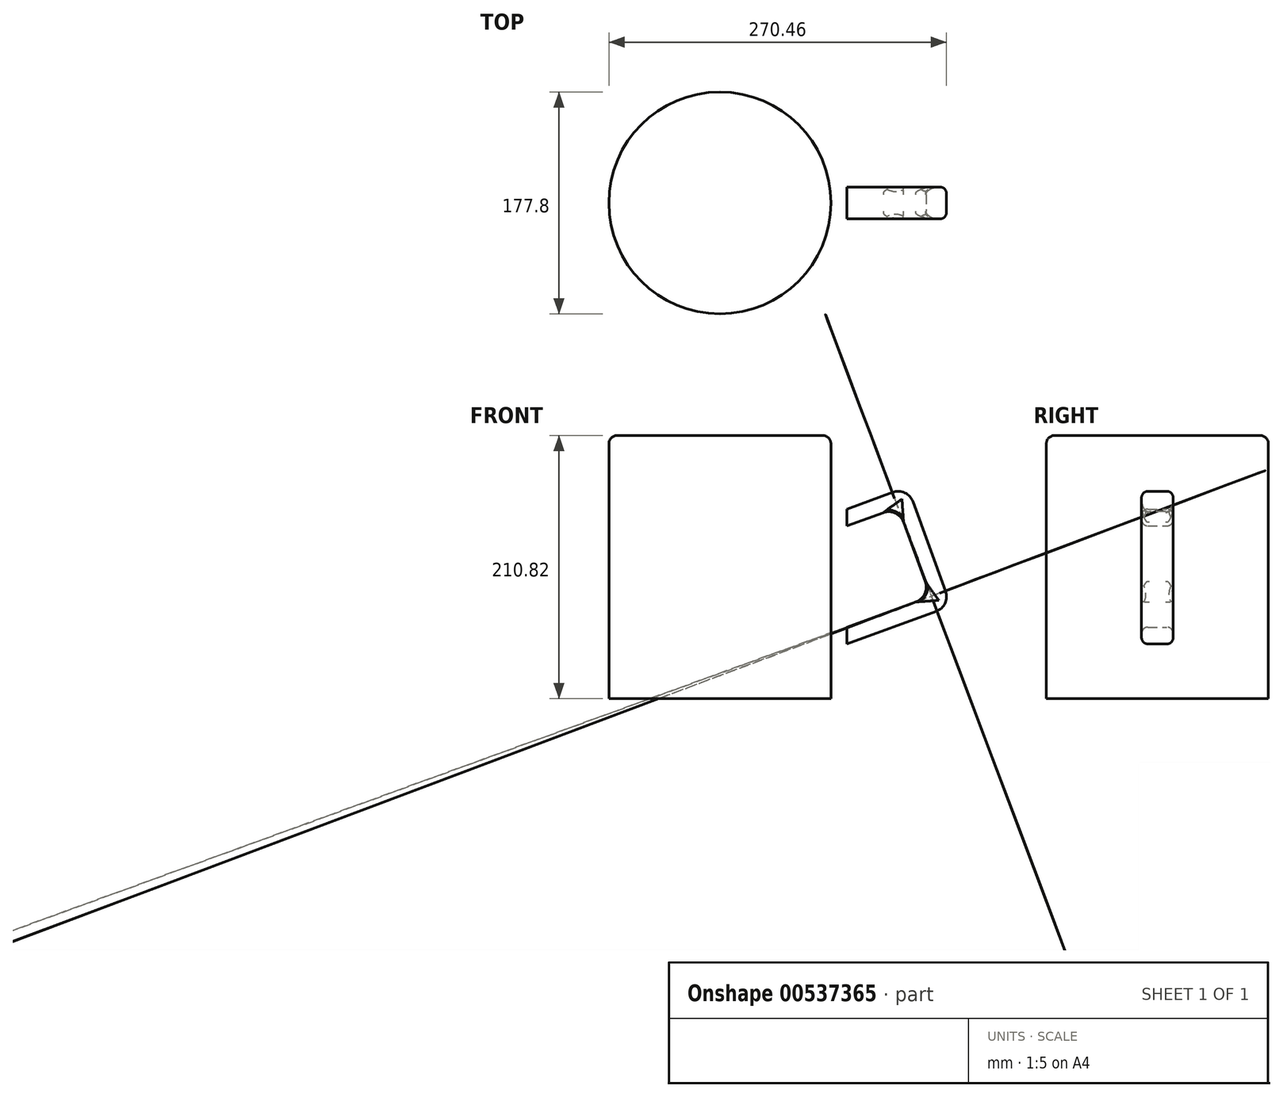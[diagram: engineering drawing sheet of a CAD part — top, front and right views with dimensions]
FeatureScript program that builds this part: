
annotation { "Feature Type Name" : "Feature", "Feature Type Description" : "" }
export const myFeature = defineFeature(function(context is Context, id is Id, definition is map)
    precondition{}
    {
        {
            var Q0;
            Q0=qCreatedBy(makeId("Front.planeOp"),FACE);
            var sketch = newSketch(context, id + "F0", { "sketchPlane" : qUnion([Q0])});
            skLineSegment(sketch, "E0.bottom", {"start": v(0, 114.3) * mm, "end": v(-101.6, 114.3) * mm});
            skLineSegment(sketch, "E0.top", {"start": v(0, -114.3) * mm, "end": v(-101.6, -114.3) * mm});
            skLineSegment(sketch, "E0.right", {"start": v(-101.6, 114.3) * mm, "end": v(-101.6, -114.3) * mm});
            skPoint(sketch, "E0.middle", {"position": v(0, 0) * mm});
            skLineSegment(sketch, "E1.bottom", {"start": v(-88.9, 114.3) * mm, "end": v(0, 114.3) * mm});
            skLineSegment(sketch, "E1.top", {"start": v(-88.9, -96.52) * mm, "end": v(0, -96.52) * mm});
            skLineSegment(sketch, "E1.left", {"start": v(-88.9, 114.3) * mm, "end": v(-88.9, -96.52) * mm});
            skLineSegment(sketch, "E2", {"start": v(0, 114.3) * mm, "end": v(0, -114.3) * mm});
            skPoint(sketch, "E0.left.end.orphan", {"position": v(101.6, -114.3) * mm});
            skPoint(sketch, "E3.orphan", {"position": v(101.6, 114.3) * mm});
            skSolve(sketch);
        }
        {
            var Q0;
            Q0=makeQuery(id+"F0.imprint","IMPRINT",FACE,{"disambiguationData":[TD([[makeQuery(id+"F0.imprint","IMPRINT",EDGE,{"derivedFrom":sQuery(id+"F0.wireOp",EDGE,"E0.bottom")}),1.0]])]});
            var Q1;
            Q1=sQuery(id+"F0.wireOp",EDGE,"E2");
            revolve(context, id + "F1", {"entities" : qUnion([Q0]), "axis" : qUnion([Q1]), "revolveType" : RevolveType.FULL});
        }
        {
            var Q0;
            Q0=makeQuery(id+"F1.opRevolve","SWEPT_EDGE",EDGE,{"disambiguationData":[OSD([sQuery(id+"F0.wireOp",EDGE,"E0.bottom"),sQuery(id+"F0.wireOp",EDGE,"E1.bottom"),sQuery(id+"F0.wireOp",EDGE,"E1.left")])]});
            var Q1;
            Q1=makeQuery(id+"F1.opRevolve","SWEPT_EDGE",EDGE,{"disambiguationData":[OSD([sQuery(id+"F0.wireOp",EDGE,"E0.bottom"),sQuery(id+"F0.wireOp",EDGE,"E0.right")])]});
            var Q2;
            Q2=makeQuery(id+"F1.opRevolve","SWEPT_EDGE",EDGE,{"disambiguationData":[OSD([sQuery(id+"F0.wireOp",EDGE,"E0.top"),sQuery(id+"F0.wireOp",EDGE,"E0.right")])]});
            fillet(context, id + "F2", {"entities" : qUnion([Q0, Q1, Q2]), "radius" : 6.35 * mm, "tangentPropagation" : true, "allowEdgeOverflow" : false});
        }
        {
            var Q0;
            Q0=qCreatedBy(makeId("Front.planeOp"),FACE);
            var sketch = newSketch(context, id + "F3", { "sketchPlane" : qUnion([Q0])});
            skLineSegment(sketch, "E4", {"start": v(101.6, 101.6) * mm, "end": v(101.6, -103.5) * mm});
            skLineSegment(sketch, "E5", {"start": v(-101.6, -101.6) * mm, "end": v(-101.6, 101.6) * mm});
            skLineSegment(sketch, "E6", {"start": v(101.6, 55.41) * mm, "end": v(150.39, 73.17) * mm});
            skLineSegment(sketch, "E7", {"start": v(150.39, 73.17) * mm, "end": v(185.14, -22.3) * mm});
            skLineSegment(sketch, "E8", {"start": v(185.14, -22.3) * mm, "end": v(101.6, -52.7) * mm});
            skLineSegment(sketch, "E9", {"start": v(101.6, 41.9) * mm, "end": v(142.8, 56.9) * mm});
            skLineSegment(sketch, "E10", {"start": v(142.8, 56.9) * mm, "end": v(168.86, -14.71) * mm});
            skLineSegment(sketch, "E11", {"start": v(168.86, -14.71) * mm, "end": v(101.6, -39.2) * mm});
            skLineSegment(sketch, "E12", {"start": v(101.6, 55.41) * mm, "end": v(101.6, -52.7) * mm});
            skSolve(sketch);
        }
        {
            var Q0;
            {var subQ2=sQuery(id+"F3.wireOp",EDGE,"E6");Q0=makeQuery(id+"F3.imprint","IMPRINT",FACE,{"disambiguationData":[TD([[makeQuery(id+"F3.imprint","IMPRINT",EDGE,{"derivedFrom":subQ2}),-1.0]])]});}
            extrude(context, id + "F4", {"entities" : qUnion([Q0]), "endBound" : BoundingType.SYMMETRIC, "depth" : 25.4 * mm, "offsetDistance" : 25.4 * mm});
        }
        {
            var Q0;
            Q0=makeQuery(id+"F4.opExtrude","CAP_EDGE",EDGE,{"disambiguationData":[OSD([sQuery(id+"F3.wireOp",EDGE,"E6")])],"isStart":false});
            var Q1;
            Q1=makeQuery(id+"F4.opExtrude","CAP_EDGE",EDGE,{"disambiguationData":[OSD([sQuery(id+"F3.wireOp",EDGE,"E7")])],"isStart":false});
            var Q2;
            Q2=makeQuery(id+"F4.opExtrude","CAP_EDGE",EDGE,{"disambiguationData":[OSD([sQuery(id+"F3.wireOp",EDGE,"E7")])],"isStart":true});
            var Q3;
            Q3=makeQuery(id+"F4.opExtrude","CAP_EDGE",EDGE,{"disambiguationData":[OSD([sQuery(id+"F3.wireOp",EDGE,"E6")])],"isStart":true});
            var Q4;
            Q4=makeQuery(id+"F4.opExtrude","CAP_EDGE",EDGE,{"disambiguationData":[OSD([sQuery(id+"F3.wireOp",EDGE,"E9")])],"isStart":false});
            var Q5;
            Q5=makeQuery(id+"F4.opExtrude","CAP_EDGE",EDGE,{"disambiguationData":[OSD([sQuery(id+"F3.wireOp",EDGE,"E10")])],"isStart":false});
            var Q6;
            Q6=makeQuery(id+"F4.opExtrude","CAP_EDGE",EDGE,{"disambiguationData":[OSD([sQuery(id+"F3.wireOp",EDGE,"E11")])],"isStart":false});
            var Q7;
            Q7=makeQuery(id+"F4.opExtrude","CAP_EDGE",EDGE,{"disambiguationData":[OSD([sQuery(id+"F3.wireOp",EDGE,"E8")])],"isStart":false});
            var Q8;
            Q8=makeQuery(id+"F4.opExtrude","CAP_EDGE",EDGE,{"disambiguationData":[OSD([sQuery(id+"F3.wireOp",EDGE,"E11")])],"isStart":true});
            var Q9;
            Q9=makeQuery(id+"F4.opExtrude","CAP_EDGE",EDGE,{"disambiguationData":[OSD([sQuery(id+"F3.wireOp",EDGE,"E8")])],"isStart":true});
            var Q10;
            Q10=makeQuery(id+"F4.opExtrude","CAP_EDGE",EDGE,{"disambiguationData":[OSD([sQuery(id+"F3.wireOp",EDGE,"E9")])],"isStart":true});
            var Q11;
            Q11=makeQuery(id+"F4.opExtrude","CAP_EDGE",EDGE,{"disambiguationData":[OSD([sQuery(id+"F3.wireOp",EDGE,"E10")])],"isStart":true});
            fillet(context, id + "F5", {"entities" : qUnion([Q0, Q1, Q2, Q3, Q4, Q5, Q6, Q7, Q8, Q9, Q10, Q11]), "radius" : 5.08 * mm, "tangentPropagation" : true, "allowEdgeOverflow" : false});
        }
        {
            var Q0;
            Q0=makeQuery(id+"F4.opExtrude","SWEPT_EDGE",EDGE,{"disambiguationData":[OSD([sQuery(id+"F3.wireOp",EDGE,"E6"),sQuery(id+"F3.wireOp",EDGE,"E7")])]});
            var Q1;
            Q1=makeQuery(id+"F4.opExtrude","SWEPT_EDGE",EDGE,{"disambiguationData":[OSD([sQuery(id+"F3.wireOp",EDGE,"E7"),sQuery(id+"F3.wireOp",EDGE,"E8")])]});
            var Q2;
            Q2=makeQuery(id+"F4.opExtrude","SWEPT_EDGE",EDGE,{"disambiguationData":[OSD([sQuery(id+"F3.wireOp",EDGE,"E9"),sQuery(id+"F3.wireOp",EDGE,"E10")])]});
            var Q3;
            Q3=makeQuery(id+"F4.opExtrude","SWEPT_EDGE",EDGE,{"disambiguationData":[OSD([sQuery(id+"F3.wireOp",EDGE,"E10"),sQuery(id+"F3.wireOp",EDGE,"E11")])]});
            fillet(context, id + "F6", {"entities" : qUnion([Q0, Q1, Q2, Q3]), "radius" : 12.7 * mm, "tangentPropagation" : true, "allowEdgeOverflow" : false});
        }
    });
